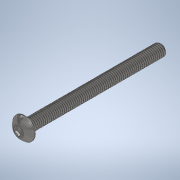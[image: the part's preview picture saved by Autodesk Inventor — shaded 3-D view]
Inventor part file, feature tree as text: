
AUTODESK INVENTOR PART (.ipt)
format: ipt  version: 2020 (Build 240168000, 168)  size: 1,135,616 bytes
history: native  units: mm (DEFAULTED — no unit token found)
features: revolve x1
ambient origin geometry x8: Origin, YZ Plane, XZ Plane, XY Plane, X Axis, Y Axis, Z Axis, Center Point
bodies: Solid1 (feature_tree)
feature tree (1):
  revolve  "Revolve2"  [1 undecoded]
note: 1 required parameter value undecoded (feature->parameter linkage not recoverable at this tier; creation-order binding heuristic only, values carry confidence <= 0.55)
